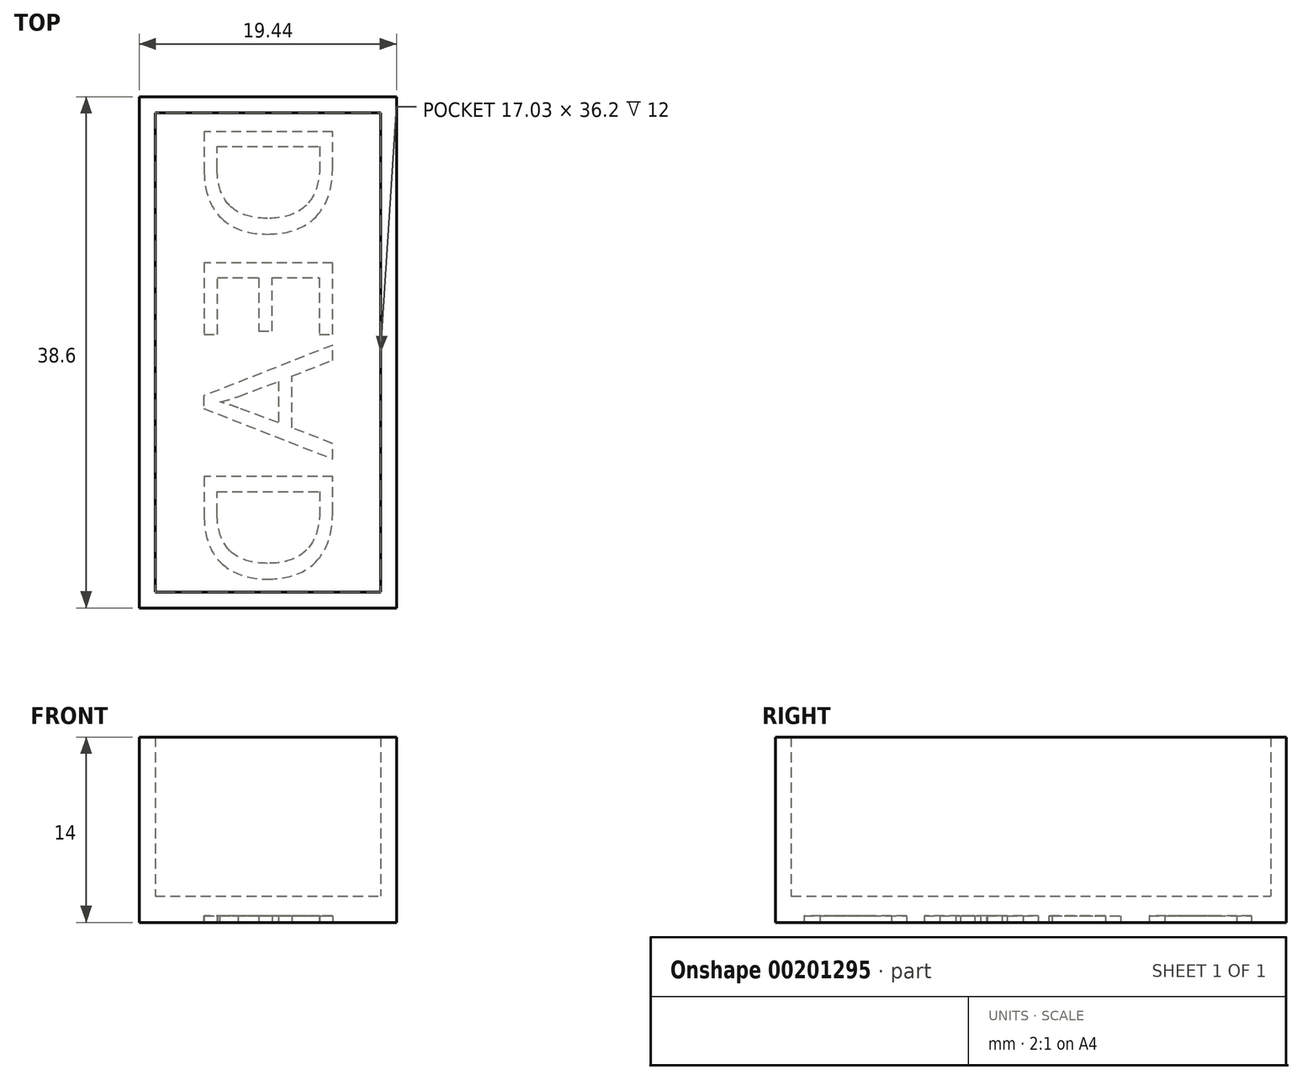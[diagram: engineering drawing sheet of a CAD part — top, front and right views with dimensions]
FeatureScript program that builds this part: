
annotation { "Feature Type Name" : "Feature", "Feature Type Description" : "" }
export const myFeature = defineFeature(function(context is Context, id is Id, definition is map)
    precondition{}
    {
        {
            var Q0;
            Q0=qCreatedBy(makeId("Top.planeOp"),FACE);
            var sketch = newSketch(context, id + "F0", { "sketchPlane" : qUnion([Q0])});
            skLineSegment(sketch, "E0.bottom", {"start": v(8.41, 18) * mm, "end": v(-8.42, 18) * mm, "construction": true});
            skLineSegment(sketch, "E0.top", {"start": v(8.42, -18) * mm, "end": v(-8.41, -18) * mm, "construction": true});
            skLineSegment(sketch, "E0.left", {"start": v(8.41, 18) * mm, "end": v(8.42, -18) * mm, "construction": true});
            skLineSegment(sketch, "E0.right", {"start": v(-8.42, 18) * mm, "end": v(-8.41, -18) * mm, "construction": true});
            skPoint(sketch, "E0.middle", {"position": v(0, 0) * mm});
            skLineSegment(sketch, "E1.0", {"start": v(8.51, 18.1) * mm, "end": v(8.51, -18.1) * mm});
            skLineSegment(sketch, "E1.1", {"start": v(8.51, 18.1) * mm, "end": v(-8.52, 18.1) * mm});
            skLineSegment(sketch, "E1.2", {"start": v(-8.52, 18.1) * mm, "end": v(-8.51, -18.1) * mm});
            skLineSegment(sketch, "E1.3", {"start": v(8.51, -18.1) * mm, "end": v(-8.51, -18.1) * mm});
            skSolve(sketch);
        }
        {
            var Q0;
            Q0=qCreatedBy(makeId("Top.planeOp"),FACE);
            var sketch = newSketch(context, id + "F1", { "sketchPlane" : qUnion([Q0])});
            skLineSegment(sketch, "E2.0.0", {"start": v(8.51, -18.1) * mm, "end": v(8.51, 18.1) * mm});
            skLineSegment(sketch, "E2.0.1", {"start": v(8.51, 18.1) * mm, "end": v(-8.52, 18.1) * mm});
            skLineSegment(sketch, "E2.0.2", {"start": v(-8.52, 18.1) * mm, "end": v(-8.51, -18.1) * mm});
            skLineSegment(sketch, "E2.0.3", {"start": v(-8.51, -18.1) * mm, "end": v(8.51, -18.1) * mm});
            skLineSegment(sketch, "E3.0", {"start": v(9.71, -19.3) * mm, "end": v(9.71, 19.3) * mm});
            skLineSegment(sketch, "E3.1", {"start": v(-9.71, -19.3) * mm, "end": v(9.71, -19.3) * mm});
            skLineSegment(sketch, "E3.2", {"start": v(-9.71, 19.3) * mm, "end": v(-9.71, -19.3) * mm});
            skLineSegment(sketch, "E3.3", {"start": v(9.71, 19.3) * mm, "end": v(-9.71, 19.3) * mm});
            skSolve(sketch);
        }
        {
            var Q0;
            Q0 = qSketchRegion(id + "F1", true);
            extrude(context, id + "F2", {"entities" : qUnion([Q0]), "depth" : 12 * mm});
        }
        {
            var Q0;
            Q0=makeQuery(id+"F2.opExtrude","CAP_FACE",FACE,{"disambiguationData":[OSD([sQuery(id+"F1.wireOp",EDGE,"E2.0.0"),sQuery(id+"F1.wireOp",EDGE,"E2.0.1"),sQuery(id+"F1.wireOp",EDGE,"E2.0.2"),sQuery(id+"F1.wireOp",EDGE,"E2.0.3"),sQuery(id+"F1.wireOp",EDGE,"E3.0"),sQuery(id+"F1.wireOp",EDGE,"E3.1"),sQuery(id+"F1.wireOp",EDGE,"E3.2"),sQuery(id+"F1.wireOp",EDGE,"E3.3")])],"isStart":true});
            var sketch = newSketch(context, id + "F3", { "sketchPlane" : qUnion([Q0])});
            skLineSegment(sketch, "E4.0.0", {"start": v(9.71, 19.3) * mm, "end": v(-9.71, 19.3) * mm});
            skLineSegment(sketch, "E4.0.1", {"start": v(-9.71, 19.3) * mm, "end": v(-9.71, -19.3) * mm});
            skLineSegment(sketch, "E4.0.2", {"start": v(-9.71, -19.3) * mm, "end": v(9.71, -19.3) * mm});
            skLineSegment(sketch, "E4.0.3", {"start": v(9.71, -19.3) * mm, "end": v(9.71, 19.3) * mm});
            skSolve(sketch);
        }
        {
            var Q0;
            Q0 = qSketchRegion(id + "F3", true);
            extrude(context, id + "F4", {"entities" : qUnion([Q0]), "operationType" : NewBodyOperationType.ADD, "depth" : 2 * mm});
        }
        {
            var Q0;
            Q0=makeQuery(id+"F4.opExtrude","CAP_FACE",FACE,{"disambiguationData":[OSD([sQuery(id+"F3.wireOp",EDGE,"E4.0.0"),sQuery(id+"F3.wireOp",EDGE,"E4.0.1"),sQuery(id+"F3.wireOp",EDGE,"E4.0.2"),sQuery(id+"F3.wireOp",EDGE,"E4.0.3")])],"isStart":false});
            var sketch = newSketch(context, id + "F5", { "sketchPlane" : qUnion([Q0])});
            skText(sketch, "E5", { "text": "DEAD", "fontName": "OpenSans-Regular.ttf"});
            const initialGuessF5  = {"E5": [0.00489, -0.018, 0, 1, 0.00978]};
            skSetInitialGuess(sketch, initialGuessF5);
            skSolve(sketch);
        }
        {
            var Q0;
            Q0 = qSketchRegion(id + "F5", true);
            extrude(context, id + "F6", {"entities" : qUnion([Q0]), "operationType" : NewBodyOperationType.REMOVE, "oppositeDirection" : true, "depth" : .5 * mm});
        }
    });
